# Revit family: QF_BPRO_BLT 1220 E_572520
name_source: partatom
category: Sonderausstattung
revit_build: Autodesk Revit 2018 (Build: 20190510_1515(x64)
units: mm (PartAtom-declared; Revit-internal decimal feet)

## family parameters
Arbeitsebenenbasiert = Nein
Beim Laden mit Abzugskörper schneiden = Nein
Bemaßung runder Anschluss = Durchmesser verwenden
Gemeinsam genutzt = Nein
Immer vertikal = Ja
Raumberechnungspunkt = Ja
Teiletyp = Normal

## types (1)
- BLT 1220 E
    Artikel Nummer = 572520
    Beschreibung = B.PROTHERM Speisentransportbehälter
aus Edelstahl
    Beschreibung durch Hersteller analog Leistungsverzeichniskurztext = Abmessungen

Länge:			540 mm
Breite:			815 mm
Höhe:			1.495 mm


Ausführung

Aufbau
Der Speisentransportbehälter besteht aus CNS 18/10, Werkstoff-Nr. 1.4301. Die Oberfläche ist mikroliert.  
Behälter und Flügeltür sind doppelwandig und mit FCKW-freiem PUR-Schaum temperaturisolierend ausgeschäumt. Der Behälter ist fahrbar mittels rostfreien Kunststoffrollen gemäß DIN 18867, Teil 8 (2 Bock- und 2 Lenkrollen mit Feststeller, Rollendurchmesser 125 mm). Die stabile Bodenkonstruktion aus Kunststoff mit integriertem, umlaufendem Stoßschutz schützt Gerät und Mobiliar vor Beschädigung.

Korpus
Die geschlossene Abdeckung des BLT 1220 E ist mit Stapelprägungen versehen, die die Stapelfähigkeit mit B.PROTHERM-Behältern aus Kunststoff erlauben.

Boden, Rück- und Seitenwände sind fugenlos verschweißt mit Kantradien R3 (Hygieneausführung H1). Die Seitenwände sind mit 20 Paar tiefgezogenen Auflagesicken im Abstand von 57,5mm zur Aufnahme von Gastronorm-Behältern der Größe GN 1/1 oder deren Unterteilung versehen. An der Rückwand des Innenkorpus befinden sich ebenfalls im Abstand von 57,5 mm Prägungen, die auch bei Bestückung mit GN-Behältern ein Zirkulieren der Heißluft und somit eine gleichmäßige Temperatur im  Behälterinnenraum ermöglichen. 
Innenkorpus mit Außenkorpus frontseitig wasserdicht verschweißt.

Der Behälter ist frontseitig mit einer um 180° schwenkbaren, bei Bedarf abnehmbaren Flügeltür ausgestattet. Tür innen glatt mit entnehmbarem, umlaufendem und lebensmittelbeständigem Dichtungsrahmen. Tür außen mit robuster Spannverschlussleiste aus CNS. In die Tür eingebaut sind eine analoge Temperaturanzeige sowie eine Feuchtigkeitsregulierung für den Behälterinnenraum.
Die Tür ist frontseitig mit einem CNS-Sicherheits-Schiebegriff mit seitlichen Stoßschutzelementen aus Kunststoff (Polyamid) ausgestattet. Der ergonomische Schiebegriff bietet zusätzliche Schutzfunktion. 

Stabile, geschlossene Bodenkonstruktion aus massivem Kunststoff mit integriertem, umlaufendem Stoßschutz.

Der Korpus ist frontseitig mit einer Kondensat-auffangrinne aus Kunststoff (Polyamid) ausgestattet, zur Vermeidung von Rutsch- und Verletzungsgefahr.

Alle Verschleißteile (wie z.B. Rollen, Schiebegriff, Verschlüsse etc.) sind im Servicefall einfach austauschbar. 


Zubehör/ Optionen

•	Zusätzlicher Stoßschutz am Dach aus massivem Kunststoff (analog Bodenplatte)
•	Dach (glatt) mit umlaufender Galerie aus CNS
•	Zusätzlicher Schiebegriff an der Geräterückseite
•	Tür nicht aushängbar
•	Eutektische Platte -3°C, aus Kunststoff (Best.Nr. 568 136)
•	Eutektische Platte -12°C, aus Kunststoff (Best.Nr. 573 332)
•	Einschubrahmen zur Unterteilung von GN-Behältern mit max. Tiefe 150 mm 
(Best.Nr. 564 352)
•	GN-Stege zum variablen Einsetzen von GN-Behältern der Größe GN 1/4, GN 1/6, GN 1/9 in den Einschubrahmen (ST 3 Best.Nr. 550 650, 
ST 5 Best.Nr. 550 651)
•	Menükartenhalterung an Tür frontseitig zur Aufnahme von Menükarten DIN A 6
•	BLT E-Menükarte mit Schlüssellochung, DIN A 6 (Best.Nr. 572 513) 
•	Spezialstift, zur Beschriftung der BLT E-Menükarten (Best.Nr. 564 361)
•	Menükarten-Box, Kunststoff (Best.Nr. 564 355)
•	Weitere Rollenoptionen siehe Gesamtpreisliste


 
Technische Daten

Werkstoff:   Chromnickelstahl 18/10,
	    Kunststoff (PA, PE-HD)
Isoliermaterial: PUR-Schaum - FCKW-frei 
Gewicht:	               83 kg
Kapazität:               max. 5x GN 1/1-200 1/1-100
Sicken:	               20 Paar Auflagesicken, Sickenabstand 57,5 mm



Besonderheit

•	wasserdichter Innenkorpus in Hygieneausführung H1, Kantradien R3
•	Rückwand Innenkorpus mit Prägungen für optimale Heißluftzirkulation
•	Korpus frontseitig mit Kondensat-Auffangrinne
•	VDE geprüft


Fabrikat

Hersteller:B.PRO
Modell:	BLT 1020 E
	B.PROTHERM
Best.Nr.	572 520
    Beschreibung durch Hersteller analog Leistungsverzeichnislangtext = Abmessungen

Länge:			540 mm
Breite:			815 mm
Höhe:			1.495 mm


Ausführung

Aufbau
Der Speisentransportbehälter besteht aus CNS 18/10, Werkstoff-Nr. 1.4301. Die Oberfläche ist mikroliert.  
Behälter und Flügeltür sind doppelwandig und mit FCKW-freiem PUR-Schaum temperaturisolierend ausgeschäumt. Der Behälter ist fahrbar mittels rostfreien Kunststoffrollen gemäß DIN 18867, Teil 8 (2 Bock- und 2 Lenkrollen mit Feststeller, Rollendurchmesser 125 mm). Die stabile Bodenkonstruktion aus Kunststoff mit integriertem, umlaufendem Stoßschutz schützt Gerät und Mobiliar vor Beschädigung.

Korpus
Die geschlossene Abdeckung des BLT 1220 E ist mit Stapelprägungen versehen, die die Stapelfähigkeit mit B.PROTHERM-Behältern aus Kunststoff erlauben.

Boden, Rück- und Seitenwände sind fugenlos verschweißt mit Kantradien R3 (Hygieneausführung H1). Die Seitenwände sind mit 20 Paar tiefgezogenen Auflagesicken im Abstand von 57,5mm zur Aufnahme von Gastronorm-Behältern der Größe GN 1/1 oder deren Unterteilung versehen. An der Rückwand des Innenkorpus befinden sich ebenfalls im Abstand von 57,5 mm Prägungen, die auch bei Bestückung mit GN-Behältern ein Zirkulieren der Heißluft und somit eine gleichmäßige Temperatur im  Behälterinnenraum ermöglichen. 
Innenkorpus mit Außenkorpus frontseitig wasserdicht verschweißt.

Der Behälter ist frontseitig mit einer um 180° schwenkbaren, bei Bedarf abnehmbaren Flügeltür ausgestattet. Tür innen glatt mit entnehmbarem, umlaufendem und lebensmittelbeständigem Dichtungsrahmen. Tür außen mit robuster Spannverschlussleiste aus CNS. In die Tür eingebaut sind eine analoge Temperaturanzeige sowie eine Feuchtigkeitsregulierung für den Behälterinnenraum.
Die Tür ist frontseitig mit einem CNS-Sicherheits-Schiebegriff mit seitlichen Stoßschutzelementen aus Kunststoff (Polyamid) ausgestattet. Der ergonomische Schiebegriff bietet zusätzliche Schutzfunktion. 

Stabile, geschlossene Bodenkonstruktion aus massivem Kunststoff mit integriertem, umlaufendem Stoßschutz.

Der Korpus ist frontseitig mit einer Kondensat-auffangrinne aus Kunststoff (Polyamid) ausgestattet, zur Vermeidung von Rutsch- und Verletzungsgefahr.

Alle Verschleißteile (wie z.B. Rollen, Schiebegriff, Verschlüsse etc.) sind im Servicefall einfach austauschbar. 


Zubehör/ Optionen

•	Zusätzlicher Stoßschutz am Dach aus massivem Kunststoff (analog Bodenplatte)
•	Dach (glatt) mit umlaufender Galerie aus CNS
•	Zusätzlicher Schiebegriff an der Geräterückseite
•	Tür nicht aushängbar
•	Eutektische Platte -3°C, aus Kunststoff (Best.Nr. 568 136)
•	Eutektische Platte -12°C, aus Kunststoff (Best.Nr. 573 332)
•	Einschubrahmen zur Unterteilung von GN-Behältern mit max. Tiefe 150 mm 
(Best.Nr. 564 352)
•	GN-Stege zum variablen Einsetzen von GN-Behältern der Größe GN 1/4, GN 1/6, GN 1/9 in den Einschubrahmen (ST 3 Best.Nr. 550 650, 
ST 5 Best.Nr. 550 651)
•	Menükartenhalterung an Tür frontseitig zur Aufnahme von Menükarten DIN A 6
•	BLT E-Menükarte mit Schlüssellochung, DIN A 6 (Best.Nr. 572 513) 
•	Spezialstift, zur Beschriftung der BLT E-Menükarten (Best.Nr. 564 361)
•	Menükarten-Box, Kunststoff (Best.Nr. 564 355)
•	Weitere Rollenoptionen siehe Gesamtpreisliste


 
Technische Daten

Werkstoff:   Chromnickelstahl 18/10,
	    Kunststoff (PA, PE-HD)
Isoliermaterial: PUR-Schaum - FCKW-frei 
Gewicht:	               83 kg
Kapazität:               max. 5x GN 1/1-200 1/1-100
Sicken:	               20 Paar Auflagesicken, Sickenabstand 57,5 mm



Besonderheit

•	wasserdichter Innenkorpus in Hygieneausführung H1, Kantradien R3
•	Rückwand Innenkorpus mit Prägungen für optimale Heißluftzirkulation
•	Korpus frontseitig mit Kondensat-Auffangrinne
•	VDE geprüft


Fabrikat

Hersteller:B.PRO
Modell:	BLT 1020 E
	B.PROTHERM
Best.Nr.	572 520
    CE Kennzeichnung = Ja
    Gerätegewicht Netto = 83.00 kg
    Großküchengerätezuordnung = Ja
    Hersteller = B.PRO GmbH
    Höhe = 1495 mm
    Internetadresse Gerätehersteller = https://www.bpro-solutions.com
    Internetadresse für Ersatzteilliste = https://www.bpro-solutions.com
    Kosten = 4209 $
    Länge Gerätebreite = 540 mm  [stored 1.77165 ft]
    Material = QF_Metal-Stainless-Steel_general
    Material Stoßschutz = QF_Plastic-Black-Matt
    Modell = BLT 1220 E
    Tiefe = 815 mm  [stored 2.67388 ft]
    Typenkommentare = Speisentransportbehälter
    URL = https://www.bpro-solutions.com
    Warnhinweise = Überschwappende und aus dem Gerät laufende Speisen können Verbrühungen verursachen; Kinder, die in leere Geräte klettern, können sich nicht selbst befreien, wenn die Gerätetüren von außen verriegelt sind; beim Schieben des Geräts können Gegenstände von der Geräteoberfläche rutschen oder das Gerät kann kippen (nur Schräge Flächen mit einer Neigung kleiner 10° befahren)
    Zubehör = Ja

note: [stored X ft] marks values corroborated as IEEE doubles in the binary element streams (Revit-internal decimal feet)
